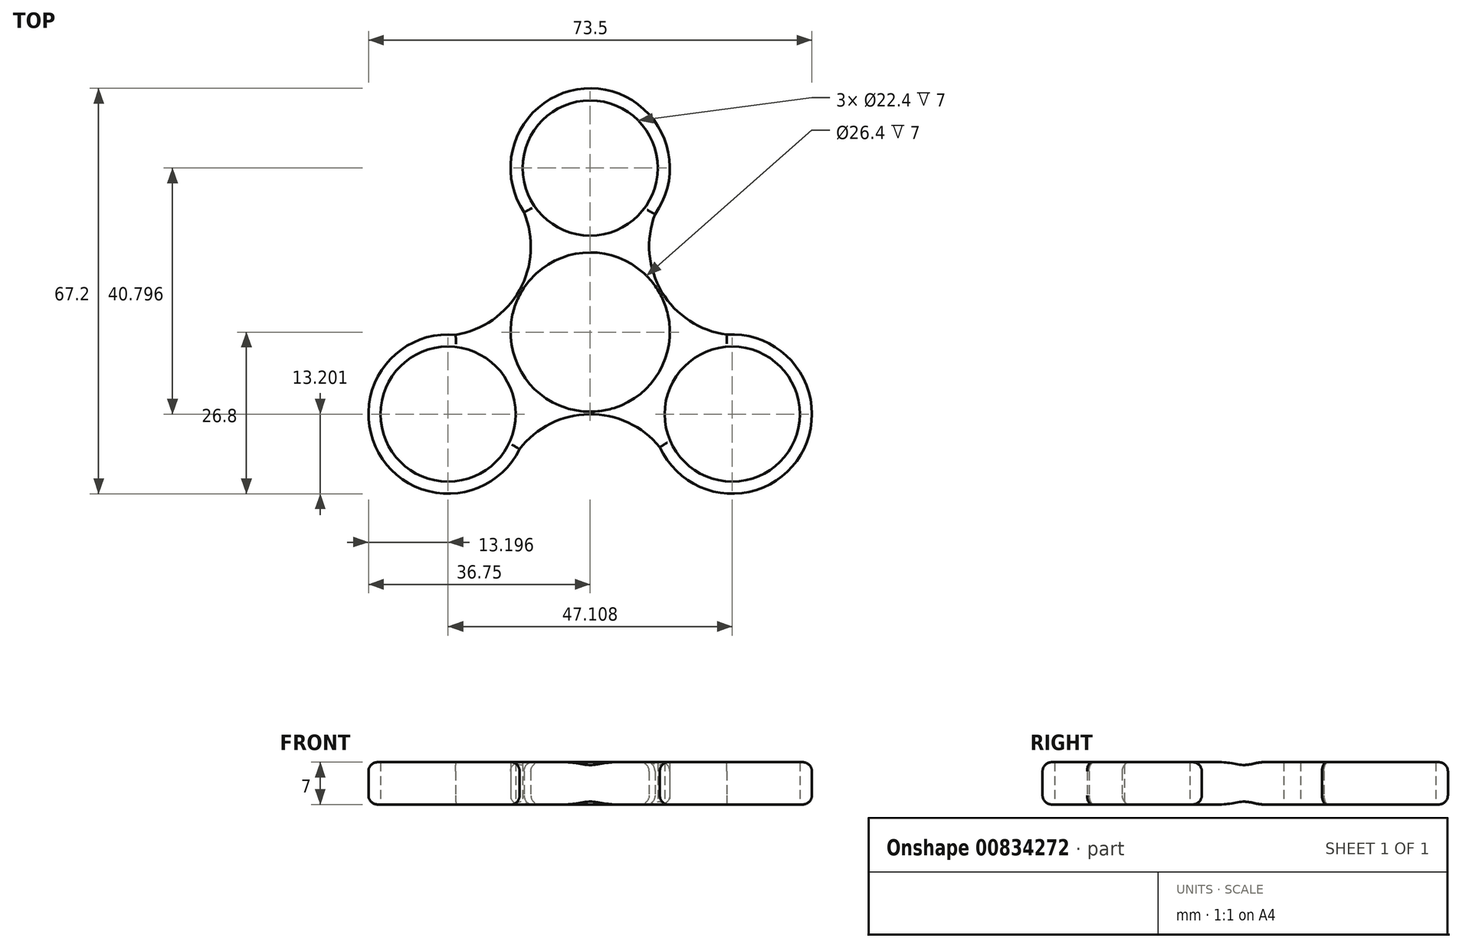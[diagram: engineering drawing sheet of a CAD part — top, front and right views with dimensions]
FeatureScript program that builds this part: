
annotation { "Feature Type Name" : "Feature", "Feature Type Description" : "" }
export const myFeature = defineFeature(function(context is Context, id is Id, definition is map)
    precondition{}
    {
        {
            var Q0;
            Q0=qCreatedBy(makeId("Top.planeOp"),FACE);
            var sketch = newSketch(context, id + "F0", { "sketchPlane" : qUnion([Q0])});
            skCircle(sketch, "E0", {"center": v(0, 0) * mm, "radius": 11.2 * mm});
            skCircle(sketch, "E1", {"center": v(0, 0) * mm, "radius": 13.2 * mm});
            skCircle(sketch, "E2", {"center": v(0, 27.2) * mm, "radius": 11.2 * mm});
            skCircle(sketch, "E3", {"center": v(0, 27.2) * mm, "radius": 13.2 * mm});
            skCircle(sketch, "E4.1.0", {"center": v(-23.55, -13.6) * mm, "radius": 11.2 * mm});
            skCircle(sketch, "E4.1.1", {"center": v(-23.55, -13.6) * mm, "radius": 13.2 * mm});
            skCircle(sketch, "E4.2.0", {"center": v(23.55, -13.6) * mm, "radius": 11.2 * mm});
            skCircle(sketch, "E4.2.1", {"center": v(23.55, -13.6) * mm, "radius": 13.2 * mm});
            skArc(sketch, "E5", {"start": v(10.75, 19.53) * mm, "mid": v(11.88, 6.67) * mm, "end": v(22.67, -0.43) * mm});
            skArc(sketch, "E6.1.0", {"start": v(-22.3, -0.46) * mm, "mid": v(-11.71, 6.95) * mm, "end": v(-10.96, 19.84) * mm});
            skArc(sketch, "E6.2.0", {"start": v(11.54, -19.08) * mm, "mid": v(-0.16, -13.62) * mm, "end": v(-11.7, -19.41) * mm});
            skSolve(sketch);
        }
        {
            var Q0;
            Q0 = qSketchRegion(id + "F0", true);
            extrude(context, id + "F1", {"entities" : qUnion([Q0]), "depth" : 7 * mm, "offsetDistance" : 25 * mm});
        }
        {
            var Q0;
            Q0=makeQuery(id+"F1.opExtrude","CAP_EDGE",EDGE,{"disambiguationData":[OSD([sQuery(id+"F0.wireOp",EDGE,"E6.2.0")])],"isStart":false});
            var Q1;
            Q1=makeQuery(id+"F1.opExtrude","CAP_EDGE",EDGE,{"disambiguationData":[OSD([sQuery(id+"F0.wireOp",EDGE,"E6.2.0")])],"isStart":true});
            fillet(context, id + "F2", {"entities" : qUnion([Q0, Q1]), "radius" : 1.5 * mm, "tangentPropagation" : true, "allowEdgeOverflow" : false});
        }
        {
            var Q0;
            Q0=makeQuery(id+"F1.opExtrude","CAP_EDGE",EDGE,{"disambiguationData":[OSD([sQuery(id+"F0.wireOp",EDGE,"E4.1.1")])],"isStart":false});
            var Q1;
            Q1=makeQuery(id+"F1.opExtrude","CAP_EDGE",EDGE,{"disambiguationData":[OSD([sQuery(id+"F0.wireOp",EDGE,"E6.1.0")])],"isStart":false});
            var Q2;
            Q2=makeQuery(id+"F1.opExtrude","CAP_EDGE",EDGE,{"disambiguationData":[OSD([sQuery(id+"F0.wireOp",EDGE,"E3")])],"isStart":false});
            var Q3;
            Q3=makeQuery(id+"F1.opExtrude","CAP_EDGE",EDGE,{"disambiguationData":[OSD([sQuery(id+"F0.wireOp",EDGE,"E5")])],"isStart":false});
            var Q4;
            Q4=makeQuery(id+"F1.opExtrude","CAP_EDGE",EDGE,{"disambiguationData":[OSD([sQuery(id+"F0.wireOp",EDGE,"E4.2.1")])],"isStart":false});
            fillet(context, id + "F3", {"entities" : qUnion([Q0, Q1, Q2, Q3, Q4]), "radius" : 1.5 * mm, "tangentPropagation" : true, "allowEdgeOverflow" : false});
        }
        {
            var Q0;
            Q0=makeQuery(id+"F1.opExtrude","CAP_EDGE",EDGE,{"disambiguationData":[OSD([sQuery(id+"F0.wireOp",EDGE,"E4.1.1")])],"isStart":true});
            var Q1;
            Q1=makeQuery(id+"F1.opExtrude","CAP_EDGE",EDGE,{"disambiguationData":[OSD([sQuery(id+"F0.wireOp",EDGE,"E4.2.1")])],"isStart":true});
            var Q2;
            Q2=makeQuery(id+"F1.opExtrude","CAP_EDGE",EDGE,{"disambiguationData":[OSD([sQuery(id+"F0.wireOp",EDGE,"E5")])],"isStart":true});
            var Q3;
            Q3=makeQuery(id+"F1.opExtrude","CAP_EDGE",EDGE,{"disambiguationData":[OSD([sQuery(id+"F0.wireOp",EDGE,"E3")])],"isStart":true});
            var Q4;
            Q4=makeQuery(id+"F1.opExtrude","CAP_EDGE",EDGE,{"disambiguationData":[OSD([sQuery(id+"F0.wireOp",EDGE,"E6.1.0")])],"isStart":true});
            fillet(context, id + "F4", {"entities" : qUnion([Q0, Q1, Q2, Q3, Q4]), "radius" : 1.5 * mm, "tangentPropagation" : true, "allowEdgeOverflow" : false});
        }
    });
